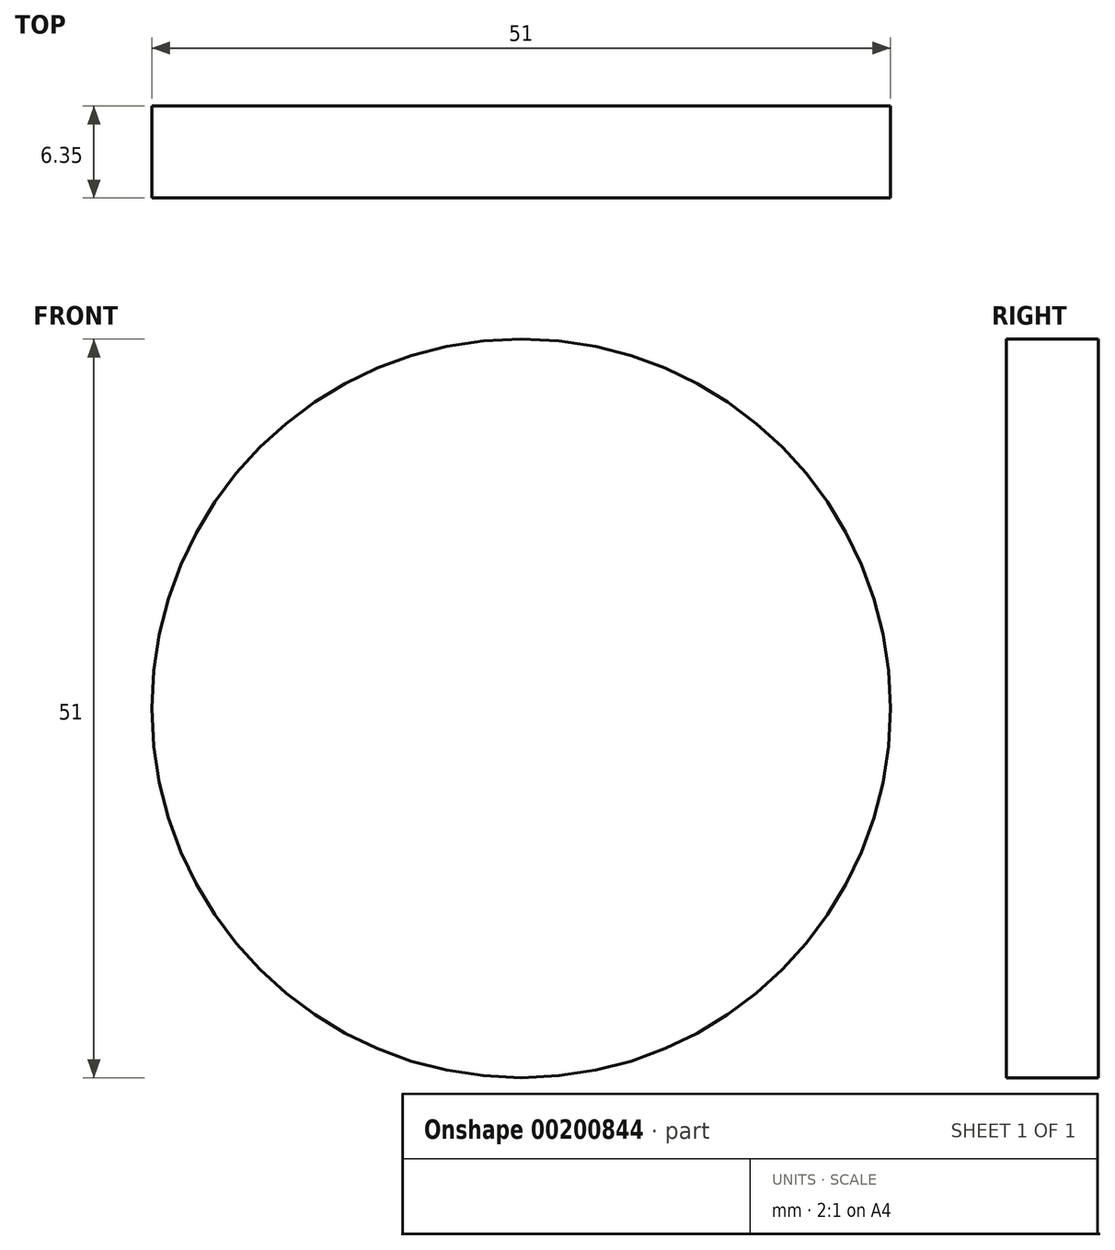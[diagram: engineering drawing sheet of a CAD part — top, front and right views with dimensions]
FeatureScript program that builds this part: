
annotation { "Feature Type Name" : "Feature", "Feature Type Description" : "" }
export const myFeature = defineFeature(function(context is Context, id is Id, definition is map)
    precondition{}
    {
        {
            var Q0;
            Q0=qCreatedBy(makeId("Front.planeOp"),FACE);
            var sketch = newSketch(context, id + "F0", { "sketchPlane" : qUnion([Q0])});
            skCircle(sketch, "E0", {"center": v(-21.99, 3.41) * mm, "radius": 25.5 * mm});
            skSolve(sketch);
        }
        {
            var Q0;
            Q0 = qSketchRegion(id + "F0", true);
            extrude(context, id + "F1", {"entities" : qUnion([Q0]), "depth" : 6.35 * mm});
        }
    });
